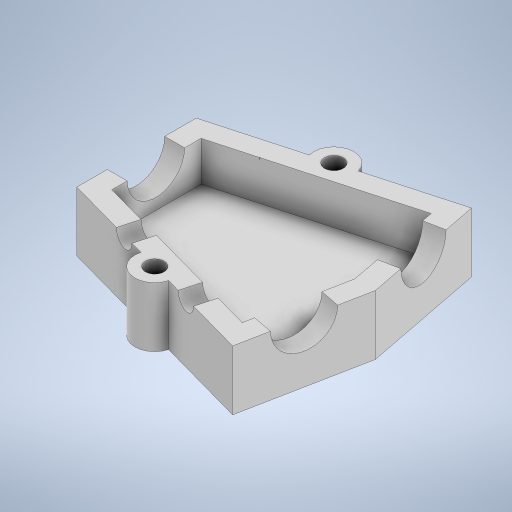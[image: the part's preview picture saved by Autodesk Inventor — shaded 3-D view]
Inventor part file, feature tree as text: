
AUTODESK INVENTOR PART (.ipt)
format: ipt  version: 2024 (Build 280153000, 153)  size: 364,032 bytes
history: native  units: in
note: dims shown in document units (in); Inventor stores cm internally (conversion verified against a paired STEP export)
features: extrude x8, sketch x8, mirror x1, projected_geometry x1
ambient origin geometry x8: Origin, YZ Plane, XZ Plane, XY Plane, X Axis, Y Axis, Z Axis, Center Point
bodies: Solid1 (feature_tree)
feature tree (18):
  extrude  "Extrusion1"  Depth=0.75in
  extrude  "Extrusion3"  Depth=0.75in
  extrude  "Extrusion4"  Depth=0.125in
  extrude  "Extrusion5"  Depth=0.375in TaperAngle=0.0deg
  extrude  "Extrusion6"  Depth=1.0in TaperAngle=0.0deg
  extrude  "Extrusion7"  Depth=1.0in TaperAngle=0.0deg
  extrude  "Extrusion8"  Depth=0.375in TaperAngle=0.0deg
  extrude  "Extrusion9"  Depth=0.375in TaperAngle=0.0deg
  mirror  "Mirror1"
  sketch  "Sketch1"  dims[d0=1.0in d1=0.75in]
  sketch  "Sketch3"  dims[d2=0.5in d3=0.75in]
  sketch  "Sketch4"  dims[d4=0.125in d5=0.125in]
  sketch  "Sketch5"  dims[d6=0.125in d7=0.375in d8=0.0in]
  sketch  "Sketch6"  dims[d12=0.36in d13=1.0in d14=0.0in]
  projected_geometry  "Projected Loop1"
  sketch  "Sketch7"  dims[d15=0.36in d16=1.0in d17=0.0in]
  sketch  "Sketch8"  dims[d18=0.36in d19=0.375in d20=0.0in]
  sketch  "Sketch10"  dims[d21=0.125in d22=0.0in d23=0.375in d24=0.0in d25=0.1181in d26=0.1181in d27=0.375in d28=0.0in d29=0.14in d30=0.14in d31=0.15in d32=0.15in d33=0.375in d34=0.0in]
